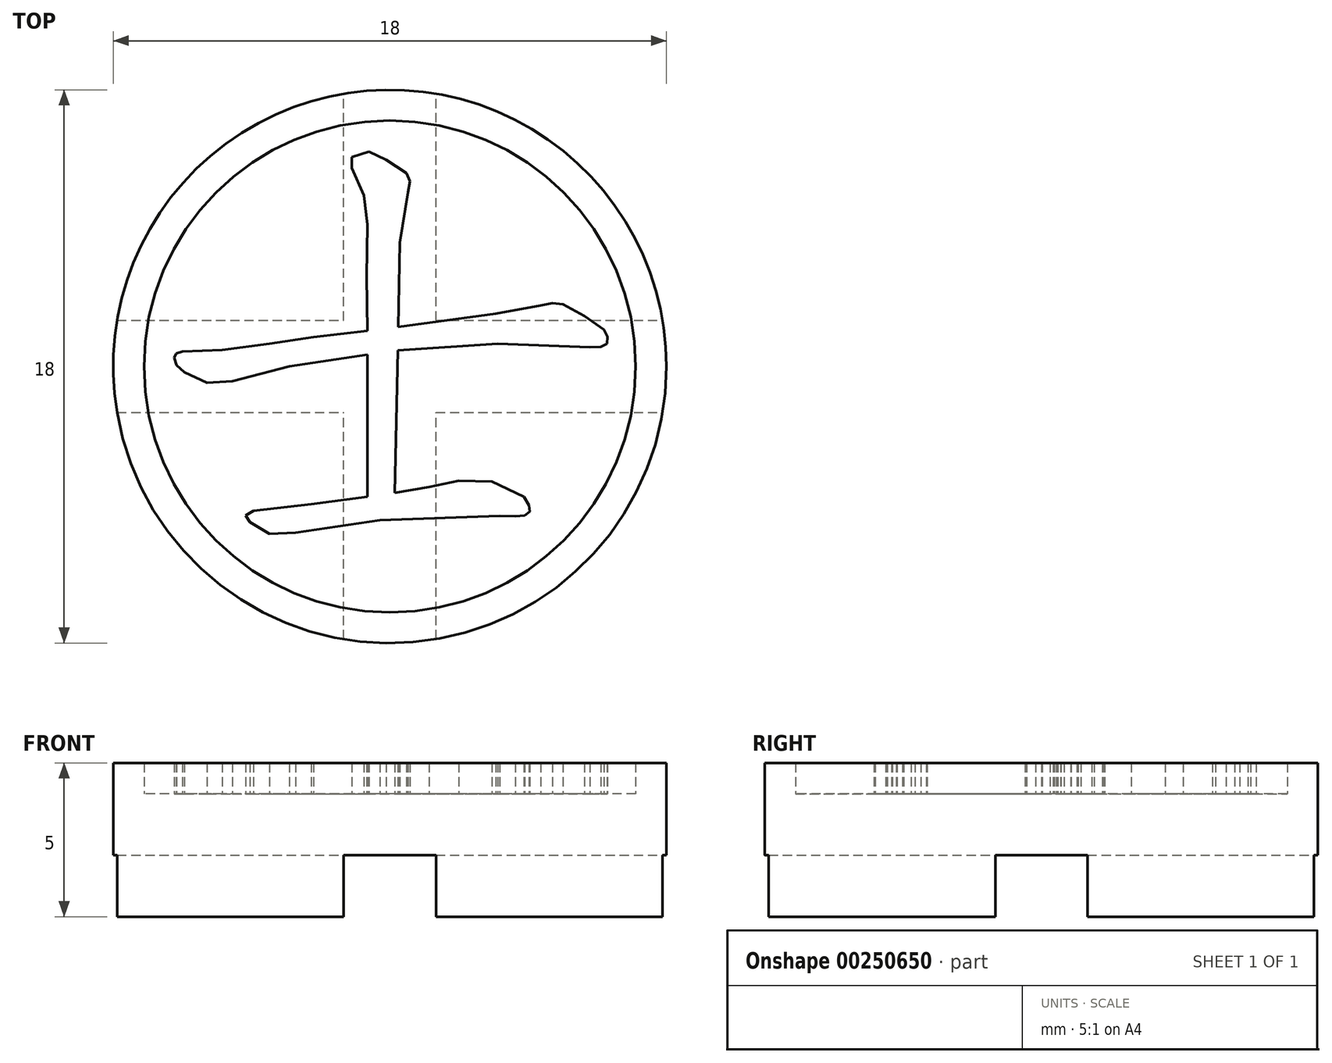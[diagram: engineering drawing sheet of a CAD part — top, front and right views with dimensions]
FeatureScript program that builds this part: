
annotation { "Feature Type Name" : "Feature", "Feature Type Description" : "" }
export const myFeature = defineFeature(function(context is Context, id is Id, definition is map)
    precondition{}
    {
        {
            var Q0;
            Q0=qCreatedBy(makeId("Top.planeOp"),FACE);
            var sketch = newSketch(context, id + "F0", { "sketchPlane" : qUnion([Q0])});
            skCircle(sketch, "E0", {"center": v(-31.33, 19.76) * mm, "radius": 9 * mm});
            skSolve(sketch);
        }
        {
            var Q0;
            Q0=qSketchRegion(id+"F0",true);
            extrude(context, id + "F1", {"entities" : qUnion([Q0]), "depth" : 4 * mm});
        }
        {
            var Q0;
            Q0=makeQuery(id+"F1.opExtrude","CAP_FACE",FACE,{"disambiguationData":[OSD([sQuery(id+"F0.wireOp",EDGE,"E0")])],"isStart":false});
            var sketch = newSketch(context, id + "F2", { "sketchPlane" : qUnion([Q0])});
            skCircle(sketch, "E1", {"center": v(-31.33, 19.76) * mm, "radius": 8 * mm});
            skCircle(sketch, "E2", {"center": v(-31.33, 19.76) * mm, "radius": 9 * mm});
            skSolve(sketch);
        }
        {
            var Q0;
            Q0=makeQuery(id+"F1.opExtrude","CAP_FACE",FACE,{"disambiguationData":[OSD([sQuery(id+"F0.wireOp",EDGE,"E0")])],"isStart":true});
            var sketch = newSketch(context, id + "F3", { "sketchPlane" : qUnion([Q0])});
            skLineSegment(sketch, "E3", {"start": v(-31.33, -19.76) * mm, "end": v(-22.33, -19.76) * mm, "construction": true});
            skLineSegment(sketch, "E4", {"start": v(-31.33, -19.76) * mm, "end": v(-31.33, -10.76) * mm, "construction": true});
            skLineSegment(sketch, "E5", {"start": v(-31.33, -19.76) * mm, "end": v(-40.33, -19.76) * mm, "construction": true});
            skLineSegment(sketch, "E6", {"start": v(-31.33, -19.76) * mm, "end": v(-31.33, -28.76) * mm, "construction": true});
            skLineSegment(sketch, "E7.bottom", {"start": v(-40.33, -28.76) * mm, "end": v(-22.33, -28.76) * mm});
            skLineSegment(sketch, "E7.top", {"start": v(-40.33, -10.76) * mm, "end": v(-22.33, -10.76) * mm});
            skLineSegment(sketch, "E7.left", {"start": v(-22.33, -10.76) * mm, "end": v(-22.33, -28.76) * mm});
            skLineSegment(sketch, "E7.right", {"start": v(-40.33, -10.76) * mm, "end": v(-40.33, -28.76) * mm});
            skPoint(sketch, "E8", {"position": v(-31.33, -28.76) * mm});
            skPoint(sketch, "E9", {"position": v(-40.33, -19.76) * mm});
            skPoint(sketch, "E10", {"position": v(-22.33, -19.76) * mm});
            skPoint(sketch, "E11", {"position": v(-31.33, -10.76) * mm});
            skLineSegment(sketch, "E12.bottom", {"start": v(-32.83, -10.76) * mm, "end": v(-29.83, -10.76) * mm});
            skLineSegment(sketch, "E12.top", {"start": v(-32.83, -28.76) * mm, "end": v(-29.83, -28.76) * mm});
            skLineSegment(sketch, "E12.left", {"start": v(-32.83, -10.76) * mm, "end": v(-32.83, -28.76) * mm});
            skLineSegment(sketch, "E12.right", {"start": v(-29.83, -10.76) * mm, "end": v(-29.83, -28.76) * mm});
            skLineSegment(sketch, "E13.bottom", {"start": v(-40.33, -18.26) * mm, "end": v(-22.33, -18.26) * mm});
            skLineSegment(sketch, "E13.top", {"start": v(-40.33, -21.26) * mm, "end": v(-22.33, -21.26) * mm});
            skLineSegment(sketch, "E13.left", {"start": v(-40.33, -18.26) * mm, "end": v(-40.33, -21.26) * mm});
            skLineSegment(sketch, "E13.right", {"start": v(-22.33, -18.26) * mm, "end": v(-22.33, -21.26) * mm});
            skSolve(sketch);
        }
        {
            var Q0;
            {var subQ1=sQuery(id+"F3.wireOp",EDGE,"E12.bottom");var subQ3=makeQuery(id+"F1.opExtrude","CAP_EDGE",EDGE,{"disambiguationData":[OSD([sQuery(id+"F0.wireOp",EDGE,"E0")])],"isStart":true});var subQ4=makeQuery(id+"F3.imprint","INTERSECT",VERTEX,{"derivedFrom":[subQ3,subQ1]});Q0=makeQuery(id+"F3.imprint","IMPRINT",FACE,{"disambiguationData":[TD([[makeQuery(id+"F3.imprint","IMPRINT",EDGE,{"disambiguationData":[TD([[subQ4,1.0]])],"derivedFrom":subQ3}),1.0]])]});}
            var Q1;
            {var subQ1=sQuery(id+"F3.wireOp",EDGE,"E12.bottom");var subQ3=makeQuery(id+"F1.opExtrude","CAP_EDGE",EDGE,{"disambiguationData":[OSD([sQuery(id+"F0.wireOp",EDGE,"E0")])],"isStart":true});var subQ4=makeQuery(id+"F3.imprint","INTERSECT",VERTEX,{"derivedFrom":[subQ3,subQ1]});Q1=makeQuery(id+"F3.imprint","IMPRINT",FACE,{"disambiguationData":[TD([[makeQuery(id+"F3.imprint","IMPRINT",EDGE,{"disambiguationData":[TD([[subQ4,-1.0]])],"derivedFrom":subQ3}),1.0]])]});}
            var Q2;
            {var subQ1=sQuery(id+"F3.wireOp",EDGE,"E12.top");var subQ3=makeQuery(id+"F1.opExtrude","CAP_EDGE",EDGE,{"disambiguationData":[OSD([sQuery(id+"F0.wireOp",EDGE,"E0")])],"isStart":true});var subQ4=makeQuery(id+"F3.imprint","INTERSECT",VERTEX,{"derivedFrom":[subQ3,subQ1]});Q2=makeQuery(id+"F3.imprint","IMPRINT",FACE,{"disambiguationData":[TD([[makeQuery(id+"F3.imprint","IMPRINT",EDGE,{"disambiguationData":[TD([[subQ4,-1.0]])],"derivedFrom":subQ3}),1.0]])]});}
            var Q3;
            {var subQ1=sQuery(id+"F3.wireOp",EDGE,"E12.top");var subQ3=makeQuery(id+"F1.opExtrude","CAP_EDGE",EDGE,{"disambiguationData":[OSD([sQuery(id+"F0.wireOp",EDGE,"E0")])],"isStart":true});var subQ4=makeQuery(id+"F3.imprint","INTERSECT",VERTEX,{"derivedFrom":[subQ3,subQ1]});Q3=makeQuery(id+"F3.imprint","IMPRINT",FACE,{"disambiguationData":[TD([[makeQuery(id+"F3.imprint","IMPRINT",EDGE,{"disambiguationData":[TD([[subQ4,1.0]])],"derivedFrom":subQ3}),1.0]])]});}
            var Q4;
            {var subQ0=sQuery(id+"F3.wireOp",EDGE,"E13.left");var subQ3=makeQuery(id+"F1.opExtrude","CAP_EDGE",EDGE,{"disambiguationData":[OSD([sQuery(id+"F0.wireOp",EDGE,"E0")])],"isStart":true});var subQ5=makeQuery(id+"F3.imprint","INTERSECT",VERTEX,{"derivedFrom":[subQ3,subQ0]});Q4=makeQuery(id+"F3.imprint","IMPRINT",FACE,{"disambiguationData":[TD([[makeQuery(id+"F3.imprint","IMPRINT",EDGE,{"disambiguationData":[TD([[subQ5,-1.0]])],"derivedFrom":subQ3}),1.0]])]});}
            var Q5;
            {var subQ0=sQuery(id+"F3.wireOp",EDGE,"E13.right");var subQ3=makeQuery(id+"F1.opExtrude","CAP_EDGE",EDGE,{"disambiguationData":[OSD([sQuery(id+"F0.wireOp",EDGE,"E0")])],"isStart":true});var subQ5=makeQuery(id+"F3.imprint","INTERSECT",VERTEX,{"derivedFrom":[subQ3,subQ0]});Q5=makeQuery(id+"F3.imprint","IMPRINT",FACE,{"disambiguationData":[TD([[makeQuery(id+"F3.imprint","IMPRINT",EDGE,{"disambiguationData":[TD([[subQ5,1.0]])],"derivedFrom":subQ3}),1.0]])]});}
            var Q6;
            {var subQ0=sQuery(id+"F3.wireOp",EDGE,"E13.left");var subQ3=makeQuery(id+"F1.opExtrude","CAP_EDGE",EDGE,{"disambiguationData":[OSD([sQuery(id+"F0.wireOp",EDGE,"E0")])],"isStart":true});var subQ5=makeQuery(id+"F3.imprint","INTERSECT",VERTEX,{"derivedFrom":[subQ3,subQ0]});Q6=makeQuery(id+"F3.imprint","IMPRINT",FACE,{"disambiguationData":[TD([[makeQuery(id+"F3.imprint","IMPRINT",EDGE,{"disambiguationData":[TD([[subQ5,1.0]])],"derivedFrom":subQ3}),1.0]])]});}
            var Q7;
            {var subQ0=sQuery(id+"F3.wireOp",EDGE,"E13.right");var subQ3=makeQuery(id+"F1.opExtrude","CAP_EDGE",EDGE,{"disambiguationData":[OSD([sQuery(id+"F0.wireOp",EDGE,"E0")])],"isStart":true});var subQ5=makeQuery(id+"F3.imprint","INTERSECT",VERTEX,{"derivedFrom":[subQ3,subQ0]});Q7=makeQuery(id+"F3.imprint","IMPRINT",FACE,{"disambiguationData":[TD([[makeQuery(id+"F3.imprint","IMPRINT",EDGE,{"disambiguationData":[TD([[subQ5,-1.0]])],"derivedFrom":subQ3}),1.0]])]});}
            var Q8;
            {var subQ3=makeQuery(id+"F1.opExtrude","CAP_EDGE",EDGE,{"disambiguationData":[OSD([sQuery(id+"F0.wireOp",EDGE,"E0")])],"isStart":true});var subQ5=sQuery(id+"F3.wireOp",EDGE,"E12.left");var subQ8=makeQuery(id+"F3.imprint","INTERSECT",VERTEX,{"disambiguationData":[OD(1.0)],"derivedFrom":[subQ3,subQ5]});Q8=makeQuery(id+"F3.imprint","IMPRINT",FACE,{"disambiguationData":[TD([[makeQuery(id+"F3.imprint","IMPRINT",EDGE,{"disambiguationData":[TD([[subQ8,-1.0]])],"derivedFrom":subQ3}),1.0]])]});}
            var Q9;
            {var subQ3=makeQuery(id+"F1.opExtrude","CAP_EDGE",EDGE,{"disambiguationData":[OSD([sQuery(id+"F0.wireOp",EDGE,"E0")])],"isStart":true});var subQ5=sQuery(id+"F3.wireOp",EDGE,"E12.right");var subQ8=makeQuery(id+"F3.imprint","INTERSECT",VERTEX,{"disambiguationData":[OD(1.0)],"derivedFrom":[subQ3,subQ5]});Q9=makeQuery(id+"F3.imprint","IMPRINT",FACE,{"disambiguationData":[TD([[makeQuery(id+"F3.imprint","IMPRINT",EDGE,{"disambiguationData":[TD([[subQ8,1.0]])],"derivedFrom":subQ3}),1.0]])]});}
            var Q10;
            {var subQ3=makeQuery(id+"F1.opExtrude","CAP_EDGE",EDGE,{"disambiguationData":[OSD([sQuery(id+"F0.wireOp",EDGE,"E0")])],"isStart":true});var subQ5=sQuery(id+"F3.wireOp",EDGE,"E12.left");var subQ8=makeQuery(id+"F3.imprint","INTERSECT",VERTEX,{"disambiguationData":[OD(0.0)],"derivedFrom":[subQ3,subQ5]});Q10=makeQuery(id+"F3.imprint","IMPRINT",FACE,{"disambiguationData":[TD([[makeQuery(id+"F3.imprint","IMPRINT",EDGE,{"disambiguationData":[TD([[subQ8,1.0]])],"derivedFrom":subQ3}),1.0]])]});}
            var Q11;
            {var subQ3=makeQuery(id+"F1.opExtrude","CAP_EDGE",EDGE,{"disambiguationData":[OSD([sQuery(id+"F0.wireOp",EDGE,"E0")])],"isStart":true});var subQ5=sQuery(id+"F3.wireOp",EDGE,"E12.right");var subQ8=makeQuery(id+"F3.imprint","INTERSECT",VERTEX,{"disambiguationData":[OD(0.0)],"derivedFrom":[subQ3,subQ5]});Q11=makeQuery(id+"F3.imprint","IMPRINT",FACE,{"disambiguationData":[TD([[makeQuery(id+"F3.imprint","IMPRINT",EDGE,{"disambiguationData":[TD([[subQ8,-1.0]])],"derivedFrom":subQ3}),1.0]])]});}
            var Q12;
            {var subQ2=sQuery(id+"F3.wireOp",EDGE,"E12.left");var subQ4=sQuery(id+"F3.wireOp",EDGE,"E13.bottom");var subQ8=makeQuery(id+"F3.imprint","INTERSECT",VERTEX,{"derivedFrom":[subQ2,subQ4]});Q12=makeQuery(id+"F3.imprint","IMPRINT",FACE,{"disambiguationData":[TD([[makeQuery(id+"F3.imprint","IMPRINT",EDGE,{"disambiguationData":[TD([[subQ8,1.0]])],"derivedFrom":subQ2}),1.0]])]});}
            var Q13;
            {var subQ1=sQuery(id+"F3.wireOp",EDGE,"E12.left");var subQ5=sQuery(id+"F3.wireOp",EDGE,"E13.bottom");var subQ6=makeQuery(id+"F3.imprint","INTERSECT",VERTEX,{"derivedFrom":[subQ1,subQ5]});Q13=makeQuery(id+"F3.imprint","IMPRINT",FACE,{"disambiguationData":[TD([[makeQuery(id+"F3.imprint","IMPRINT",EDGE,{"disambiguationData":[TD([[subQ6,-1.0]])],"derivedFrom":subQ1}),-1.0]])]});}
            var Q14;
            {var subQ0=sQuery(id+"F3.wireOp",EDGE,"E13.top");var subQ1=sQuery(id+"F3.wireOp",EDGE,"E12.left");var subQ2=makeQuery(id+"F3.imprint","INTERSECT",VERTEX,{"derivedFrom":[subQ1,subQ0]});Q14=makeQuery(id+"F3.imprint","IMPRINT",FACE,{"disambiguationData":[TD([[makeQuery(id+"F3.imprint","IMPRINT",EDGE,{"disambiguationData":[TD([[subQ2,-1.0]])],"derivedFrom":subQ1}),1.0]])]});}
            var Q15;
            {var subQ2=sQuery(id+"F3.wireOp",EDGE,"E13.bottom");var subQ5=sQuery(id+"F3.wireOp",EDGE,"E12.right");var subQ8=makeQuery(id+"F3.imprint","INTERSECT",VERTEX,{"derivedFrom":[subQ5,subQ2]});Q15=makeQuery(id+"F3.imprint","IMPRINT",FACE,{"disambiguationData":[TD([[makeQuery(id+"F3.imprint","IMPRINT",EDGE,{"disambiguationData":[TD([[subQ8,-1.0]])],"derivedFrom":subQ5}),1.0]])]});}
            var Q16;
            {var subQ0=sQuery(id+"F3.wireOp",EDGE,"E13.bottom");var subQ1=sQuery(id+"F3.wireOp",EDGE,"E12.left");var subQ2=makeQuery(id+"F3.imprint","INTERSECT",VERTEX,{"derivedFrom":[subQ1,subQ0]});Q16=makeQuery(id+"F3.imprint","IMPRINT",FACE,{"disambiguationData":[TD([[makeQuery(id+"F3.imprint","IMPRINT",EDGE,{"disambiguationData":[TD([[subQ2,-1.0]])],"derivedFrom":subQ1}),1.0]])]});}
            extrude(context, id + "F4", {"entities" : qUnion([Q0, Q1, Q2, Q3, Q4, Q5, Q6, Q7, Q8, Q9, Q10, Q11, Q12, Q13, Q14, Q15, Q16]), "operationType" : NewBodyOperationType.REMOVE, "oppositeDirection" : true, "depth" : 2 * mm});
        }
        {
            var Q0;
            Q0=qSketchRegion(id+"F2",true);
            var Q1;
            Q1=makeQuery(id+"F2.imprint","IMPRINT",FACE,{"disambiguationData":[TD([[makeQuery(id+"F2.imprint","IMPRINT",EDGE,{"derivedFrom":sQuery(id+"F2.wireOp",EDGE,"hKqnuJLd-dfdz-vJIs-yDKo-c4hLNRw30SuP")}),-1.0]])]});
            extrude(context, id + "F5", {"entities" : qUnion([Q0, Q1]), "operationType" : NewBodyOperationType.ADD, "depth" : 1 * mm});
        }
        {
            var Q0;
            Q0=makeQuery(id+"F1.opExtrude","CAP_FACE",FACE,{"disambiguationData":[OSD([sQuery(id+"F0.wireOp",EDGE,"E0")])],"isStart":false});
            var sketch = newSketch(context, id + "F6", { "sketchPlane" : qUnion([Q0])});
            skLineSegment(sketch, "E14", {"start": v(-32.06, 15.52) * mm, "end": v(-33.9, 15.28) * mm});
            skLineSegment(sketch, "E15", {"start": v(-33.9, 15.28) * mm, "end": v(-35.77, 15.06) * mm});
            skLineSegment(sketch, "E16", {"start": v(-35.77, 15.06) * mm, "end": v(-36.03, 14.91) * mm});
            skLineSegment(sketch, "E17", {"start": v(-36.03, 14.91) * mm, "end": v(-35.88, 14.7) * mm});
            skLineSegment(sketch, "E18", {"start": v(-35.88, 14.7) * mm, "end": v(-35.25, 14.31) * mm});
            skLineSegment(sketch, "E19", {"start": v(-35.25, 14.31) * mm, "end": v(-34.4, 14.35) * mm});
            skLineSegment(sketch, "E20", {"start": v(-34.4, 14.35) * mm, "end": v(-31.65, 14.75) * mm});
            skLineSegment(sketch, "E21", {"start": v(-31.65, 14.75) * mm, "end": v(-27.75, 14.9) * mm});
            skLineSegment(sketch, "E22", {"start": v(-27.75, 14.9) * mm, "end": v(-27.24, 14.88) * mm});
            skLineSegment(sketch, "E23", {"start": v(-27.24, 14.88) * mm, "end": v(-26.94, 14.91) * mm});
            skLineSegment(sketch, "E24", {"start": v(-26.94, 14.91) * mm, "end": v(-26.78, 15.04) * mm});
            skLineSegment(sketch, "E25", {"start": v(-26.78, 15.04) * mm, "end": v(-26.8, 15.24) * mm});
            skLineSegment(sketch, "E26", {"start": v(-26.8, 15.24) * mm, "end": v(-26.97, 15.52) * mm});
            skLineSegment(sketch, "E27", {"start": v(-26.97, 15.52) * mm, "end": v(-28.02, 16.01) * mm});
            skLineSegment(sketch, "E28", {"start": v(-28.02, 16.01) * mm, "end": v(-29.09, 16.04) * mm});
            skLineSegment(sketch, "E29", {"start": v(-29.09, 16.04) * mm, "end": v(-30.06, 15.84) * mm});
            skLineSegment(sketch, "E30", {"start": v(-30.06, 15.84) * mm, "end": v(-31.17, 15.65) * mm});
            skLineSegment(sketch, "E31", {"start": v(-31.17, 15.65) * mm, "end": v(-31.07, 20.28) * mm});
            skLineSegment(sketch, "E32", {"start": v(-31.07, 20.28) * mm, "end": v(-27.82, 20.5) * mm});
            skLineSegment(sketch, "E33", {"start": v(-27.82, 20.5) * mm, "end": v(-24.82, 20.39) * mm});
            skLineSegment(sketch, "E34", {"start": v(-24.82, 20.39) * mm, "end": v(-24.47, 20.4) * mm});
            skLineSegment(sketch, "E35", {"start": v(-24.47, 20.4) * mm, "end": v(-24.27, 20.5) * mm});
            skLineSegment(sketch, "E36", {"start": v(-24.27, 20.5) * mm, "end": v(-24.25, 20.73) * mm});
            skLineSegment(sketch, "E37", {"start": v(-24.25, 20.73) * mm, "end": v(-24.37, 20.95) * mm});
            skLineSegment(sketch, "E38", {"start": v(-24.37, 20.95) * mm, "end": v(-25, 21.4) * mm});
            skLineSegment(sketch, "E39", {"start": v(-25, 21.4) * mm, "end": v(-25.7, 21.79) * mm});
            skLineSegment(sketch, "E40", {"start": v(-25.7, 21.79) * mm, "end": v(-26.04, 21.82) * mm});
            skLineSegment(sketch, "E41", {"start": v(-26.04, 21.82) * mm, "end": v(-26.42, 21.74) * mm});
            skLineSegment(sketch, "E42", {"start": v(-26.42, 21.74) * mm, "end": v(-27.89, 21.48) * mm});
            skLineSegment(sketch, "E43", {"start": v(-27.89, 21.48) * mm, "end": v(-31.06, 21.05) * mm});
            skLineSegment(sketch, "E44", {"start": v(-31.06, 21.05) * mm, "end": v(-31, 23.8) * mm});
            skLineSegment(sketch, "E45", {"start": v(-31, 23.8) * mm, "end": v(-30.74, 25.43) * mm});
            skLineSegment(sketch, "E46", {"start": v(-30.74, 25.43) * mm, "end": v(-30.68, 25.78) * mm});
            skLineSegment(sketch, "E47", {"start": v(-30.68, 25.78) * mm, "end": v(-30.79, 26.05) * mm});
            skLineSegment(sketch, "E48", {"start": v(-30.79, 26.05) * mm, "end": v(-31.45, 26.48) * mm});
            skLineSegment(sketch, "E49", {"start": v(-31.45, 26.48) * mm, "end": v(-32, 26.75) * mm});
            skLineSegment(sketch, "E50", {"start": v(-32, 26.75) * mm, "end": v(-32.57, 26.57) * mm});
            skLineSegment(sketch, "E51", {"start": v(-32.57, 26.57) * mm, "end": v(-32.57, 26.22) * mm});
            skLineSegment(sketch, "E52", {"start": v(-32.57, 26.22) * mm, "end": v(-32.18, 25.32) * mm});
            skLineSegment(sketch, "E53", {"start": v(-32.18, 25.32) * mm, "end": v(-32.06, 24.37) * mm});
            skLineSegment(sketch, "E54", {"start": v(-32.06, 24.37) * mm, "end": v(-32.09, 22.68) * mm});
            skLineSegment(sketch, "E55", {"start": v(-32.09, 22.68) * mm, "end": v(-32.06, 20.92) * mm});
            skLineSegment(sketch, "E56", {"start": v(-32.06, 20.92) * mm, "end": v(-33.8, 20.7) * mm});
            skLineSegment(sketch, "E57", {"start": v(-33.8, 20.7) * mm, "end": v(-35.25, 20.5) * mm});
            skLineSegment(sketch, "E58", {"start": v(-35.25, 20.5) * mm, "end": v(-36.8, 20.3) * mm});
            skLineSegment(sketch, "E59", {"start": v(-36.8, 20.3) * mm, "end": v(-38.08, 20.24) * mm});
            skLineSegment(sketch, "E60", {"start": v(-38.08, 20.24) * mm, "end": v(-38.28, 20.18) * mm});
            skLineSegment(sketch, "E61", {"start": v(-38.28, 20.18) * mm, "end": v(-38.35, 20.04) * mm});
            skLineSegment(sketch, "E62", {"start": v(-38.35, 20.04) * mm, "end": v(-38.27, 19.8) * mm});
            skLineSegment(sketch, "E63", {"start": v(-38.27, 19.8) * mm, "end": v(-38.01, 19.57) * mm});
            skLineSegment(sketch, "E64", {"start": v(-38.01, 19.57) * mm, "end": v(-37.28, 19.23) * mm});
            skLineSegment(sketch, "E65", {"start": v(-37.28, 19.23) * mm, "end": v(-36.45, 19.28) * mm});
            skLineSegment(sketch, "E66", {"start": v(-36.45, 19.28) * mm, "end": v(-34.6, 19.76) * mm});
            skLineSegment(sketch, "E67", {"start": v(-34.6, 19.76) * mm, "end": v(-32.06, 20.15) * mm});
            skLineSegment(sketch, "E68", {"start": v(-32.06, 20.15) * mm, "end": v(-32.06, 15.52) * mm});
            skSolve(sketch);
        }
        {
            var Q0;
            Q0 = qSketchRegion(id + "F6", true);
            extrude(context, id + "F7", {"entities" : qUnion([Q0]), "operationType" : NewBodyOperationType.ADD, "depth" : 1 * mm});
        }
    });
